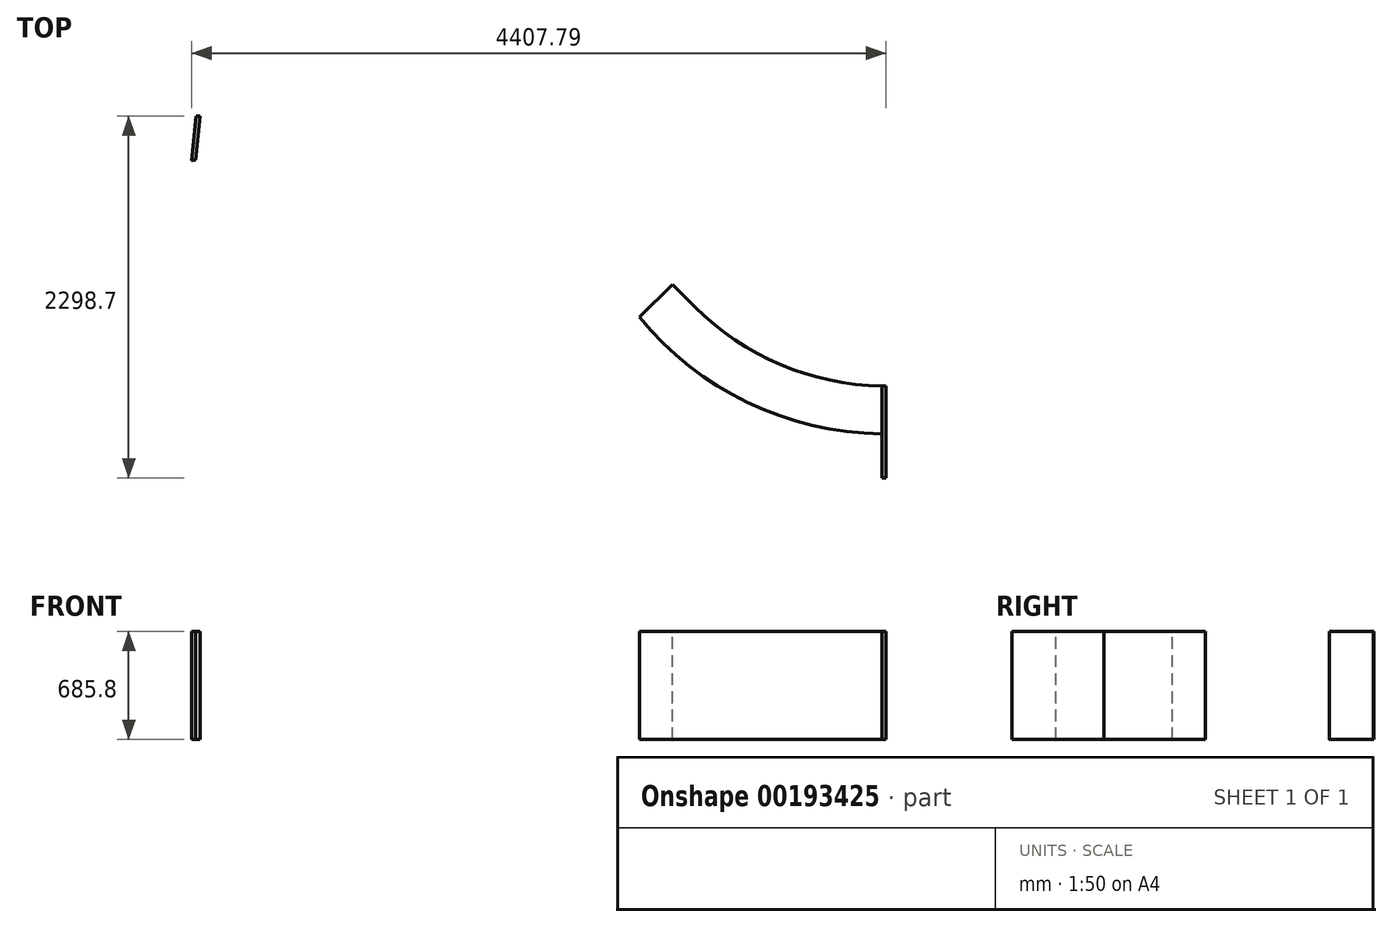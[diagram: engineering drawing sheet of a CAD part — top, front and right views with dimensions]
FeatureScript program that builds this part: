
annotation { "Feature Type Name" : "Feature", "Feature Type Description" : "" }
export const myFeature = defineFeature(function(context is Context, id is Id, definition is map)
    precondition{}
    {
        {
            var Q0;
            Q0=qCreatedBy(makeId("Top.planeOp"),FACE);
            var sketch = newSketch(context, id + "F0", { "sketchPlane" : qUnion([Q0])});
            skLineSegment(sketch, "E0", {"start": v(-2316.67, 127.82) * mm, "end": v(349.93, 127.82) * mm});
            skLineSegment(sketch, "E1", {"start": v(2064.43, -1586.68) * mm, "end": v(2064.43, -2196.28) * mm});
            skArc(sketch, "E2", {"start": v(2064.43, -1586.68) * mm, "mid": v(852.1, -1084.52) * mm, "end": v(349.93, 127.82) * mm});
            skArc(sketch, "E3.0", {"start": v(2064.43, -1891.48) * mm, "mid": v(1189.8, -1692.24) * mm, "end": v(487.77, -1133.82) * mm});
            skArc(sketch, "E4.0", {"start": v(2064.43, -2196.28) * mm, "mid": v(1057.78, -1966.96) * mm, "end": v(249.79, -1324.25) * mm});
            skLineSegment(sketch, "E5", {"start": v(-2316.67, 127.82) * mm, "end": v(-2345.78, -179.16) * mm});
            skPoint(sketch, "E6", {"position": v(-2316.67, 127.82) * mm});
            skArc(sketch, "E7", {"start": v(487.77, -1133.82) * mm, "mid": v(-608.98, -238.62) * mm, "end": v(-1976.45, 127.82) * mm});
            skArc(sketch, "E8.0", {"start": v(249.79, -1324.25) * mm, "mid": v(-907.75, -433.81) * mm, "end": v(-2345.78, -179.16) * mm});
            skPoint(sketch, "E9.orphan", {"position": v(-2436.3, -1133.82) * mm});
            skLineSegment(sketch, "E10.0", {"start": v(-2291.3, 126.27) * mm, "end": v(-2317.7, -152.02) * mm});
            skArc(sketch, "E11.0", {"start": v(300.99, -1348.25) * mm, "mid": v(-872.47, -421.75) * mm, "end": v(-2343.36, -153.55) * mm});
            skArc(sketch, "E12.0", {"start": v(2064.43, -2170.88) * mm, "mid": v(1097.91, -1957.81) * mm, "end": v(310.57, -1358.11) * mm});
            skLineSegment(sketch, "E13.0", {"start": v(2039.03, -1586.5) * mm, "end": v(2039.03, -2170.74) * mm});
            skLineSegment(sketch, "E14", {"start": v(2064.43, 127.82) * mm, "end": v(0, -1936.6) * mm});
            skLineSegment(sketch, "E15", {"start": v(852.1, -1084.52) * mm, "end": v(708.4, -940.83) * mm});
            skLineSegment(sketch, "E16.MirrorCS", {"start": v(588.36, -1635.62) * mm, "end": v(589.05, -1634.93) * mm});
            skLineSegment(sketch, "E17.MirrorCS", {"start": v(852.1, -1084.52) * mm, "end": v(995.78, -1228.2) * mm});
            skLineSegment(sketch, "E18", {"start": v(-2343.36, -153.55) * mm, "end": v(-2316.67, 127.82) * mm});
            skLineSegment(sketch, "E19", {"start": v(-2343.36, -153.55) * mm, "end": v(-2317.7, -152.02) * mm});
            skLineSegment(sketch, "E20", {"start": v(-2291.3, 126.27) * mm, "end": v(-2316.67, 127.82) * mm});
            skLineSegment(sketch, "E21.bottom", {"start": v(2039.03, -1586.5) * mm, "end": v(2064.43, -1586.5) * mm});
            skLineSegment(sketch, "E21.top", {"start": v(2039.03, -1586.68) * mm, "end": v(2064.43, -1586.68) * mm});
            skLineSegment(sketch, "E21.left", {"start": v(2039.03, -1586.5) * mm, "end": v(2039.03, -1586.68) * mm});
            skLineSegment(sketch, "E21.right", {"start": v(2064.43, -1586.5) * mm, "end": v(2064.43, -1586.68) * mm});
            skLineSegment(sketch, "E22", {"start": v(2064.43, -2170.88) * mm, "end": v(2039.03, -2170.74) * mm});
            skLineSegment(sketch, "E23", {"start": v(300.99, -1348.25) * mm, "end": v(310.57, -1358.11) * mm});
            skLineSegment(sketch, "E24", {"start": v(708.4, -940.83) * mm, "end": v(331.24, -1318) * mm});
            skLineSegment(sketch, "E25", {"start": v(331.24, -1318) * mm, "end": v(618.6, -1605.37) * mm});
            skLineSegment(sketch, "E26.trimOffspring", {"start": v(618.6, -1605.37) * mm, "end": v(995.78, -1228.2) * mm});
            skSolve(sketch);
        }
        {
            var Q0;
            {var subQ3=sQuery(id+"F0.wireOp",EDGE,"E22");Q0=makeQuery(id+"F0.imprint","IMPRINT",FACE,{"disambiguationData":[TD([[makeQuery(id+"F0.imprint","IMPRINT",EDGE,{"derivedFrom":subQ3}),-1.0]])]});}
            var Q1;
            {var subQ0=sQuery(id+"F0.wireOp",EDGE,"E21.top");Q1=makeQuery(id+"F0.imprint","IMPRINT",FACE,{"disambiguationData":[TD([[makeQuery(id+"F0.imprint","IMPRINT",EDGE,{"derivedFrom":subQ0}),-1.0]])]});}
            extrude(context, id + "F1", {"entities" : qUnion([Q0, Q1]), "oppositeDirection" : true, "depth" : 685.8 * mm});
        }
        {
            var Q0;
            Q0=makeQuery(id+"F0.imprint","IMPRINT",FACE,{"disambiguationData":[TD([[makeQuery(id+"F0.imprint","IMPRINT",EDGE,{"derivedFrom":sQuery(id+"F0.wireOp",EDGE,"E5")}),1.0]])]});
            var Q1;
            {var subQ5=sQuery(id+"F0.wireOp",EDGE,"E1");var subQ7=sQuery(id+"F0.wireOp",EDGE,"E4.0");var subQ8=makeQuery(id+"F0.imprint","INTERSECT",VERTEX,{"derivedFrom":[subQ5,subQ7]});Q1=makeQuery(id+"F0.imprint","IMPRINT",FACE,{"disambiguationData":[TD([[makeQuery(id+"F0.imprint","IMPRINT",EDGE,{"disambiguationData":[TD([[subQ8,-1.0]])],"derivedFrom":subQ7}),-1.0]])]});}
            extrude(context, id + "F2", {"entities" : qUnion([Q0, Q1]), "oppositeDirection" : true, "depth" : 685.8 * mm});
        }
        {
            var Q0;
            {var subQ0=sQuery(id+"F0.wireOp",EDGE,"E10.0");Q0=makeQuery(id+"F0.imprint","IMPRINT",FACE,{"disambiguationData":[TD([[makeQuery(id+"F0.imprint","IMPRINT",EDGE,{"derivedFrom":subQ0}),-1.0]])]});}
            extrude(context, id + "F3", {"entities" : qUnion([Q0]), "oppositeDirection" : true, "depth" : 685.8 * mm});
        }
        {
            var Q0;
            {var subQ5=sQuery(id+"F0.wireOp",EDGE,"E15");Q0=makeQuery(id+"F0.imprint","IMPRINT",FACE,{"disambiguationData":[TD([[makeQuery(id+"F0.imprint","IMPRINT",EDGE,{"derivedFrom":subQ5}),1.0]])]});}
            var Q1;
            {var subQ5=sQuery(id+"F0.wireOp",EDGE,"E17.MirrorCS");Q1=makeQuery(id+"F0.imprint","IMPRINT",FACE,{"disambiguationData":[TD([[makeQuery(id+"F0.imprint","IMPRINT",EDGE,{"derivedFrom":subQ5}),-1.0]])]});}
            var Q2;
            {var subQ0=sQuery(id+"F0.wireOp",EDGE,"E14");var subQ1=sQuery(id+"F0.wireOp",EDGE,"E3.0");var subQ2=makeQuery(id+"F0.imprint","INTERSECT",VERTEX,{"derivedFrom":[subQ1,subQ0]});Q2=makeQuery(id+"F0.imprint","IMPRINT",FACE,{"disambiguationData":[TD([[makeQuery(id+"F0.imprint","IMPRINT",EDGE,{"disambiguationData":[TD([[subQ2,-1.0]])],"derivedFrom":subQ1}),1.0]])]});}
            var Q3;
            {var subQ0=sQuery(id+"F0.wireOp",EDGE,"E26.trimOffspring");var subQ1=sQuery(id+"F0.wireOp",EDGE,"E3.0");var subQ2=makeQuery(id+"F0.imprint","INTERSECT",VERTEX,{"derivedFrom":[subQ1,subQ0]});Q3=makeQuery(id+"F0.imprint","IMPRINT",FACE,{"disambiguationData":[TD([[makeQuery(id+"F0.imprint","IMPRINT",EDGE,{"disambiguationData":[TD([[subQ2,-1.0]])],"derivedFrom":subQ1}),1.0]])]});}
            extrude(context, id + "F4", {"entities" : qUnion([Q0, Q1, Q2, Q3]), "oppositeDirection" : true, "depth" : 685.8 * mm});
        }
    });
